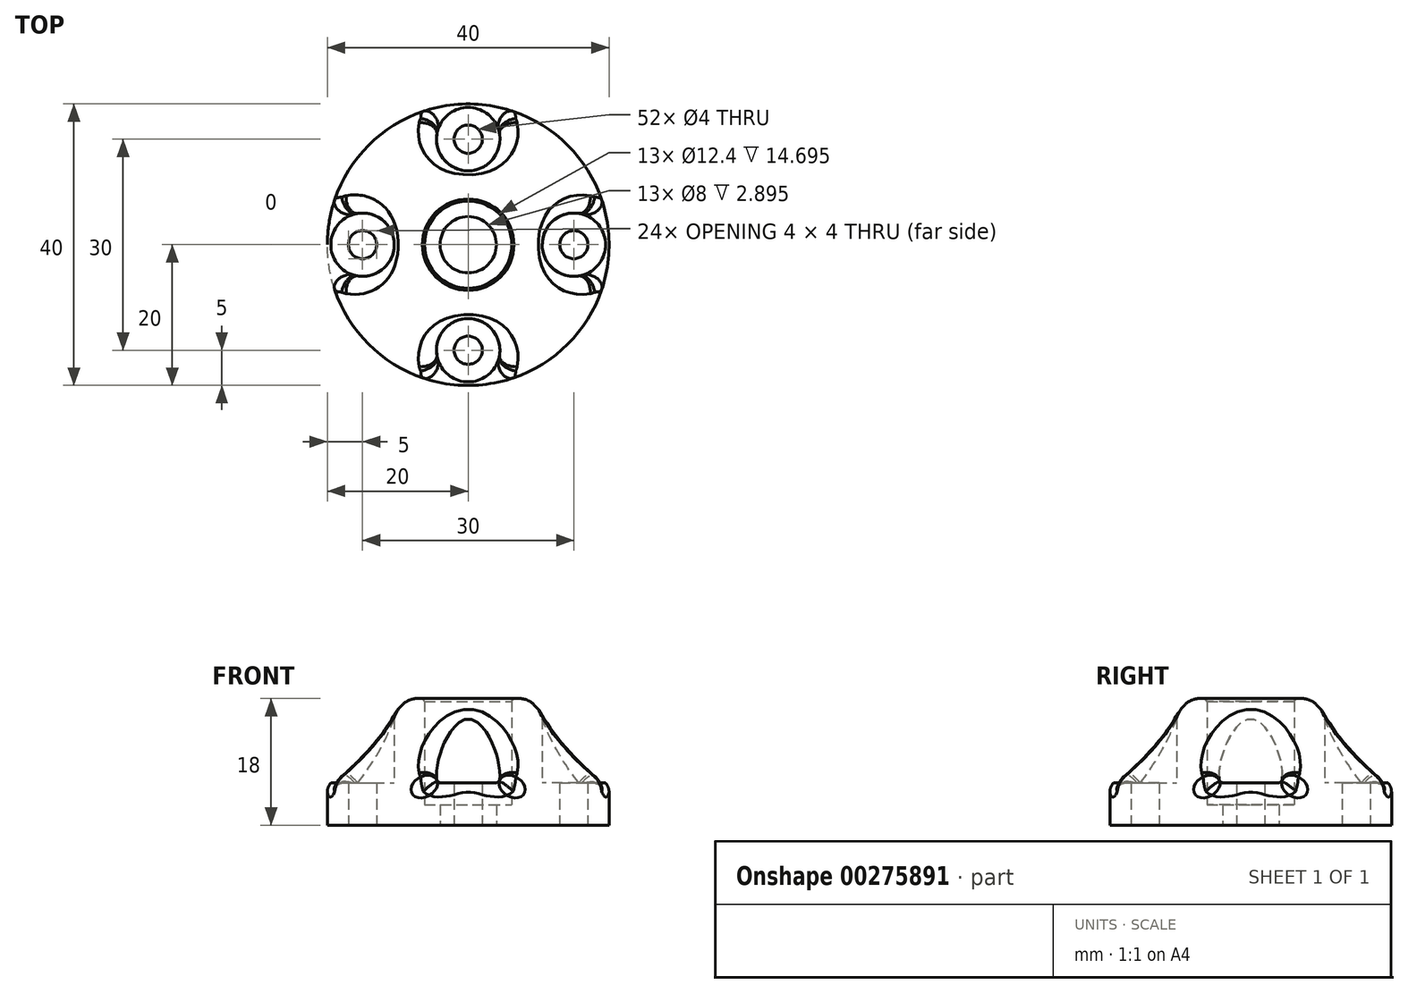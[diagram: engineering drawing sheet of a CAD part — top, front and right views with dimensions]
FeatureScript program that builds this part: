
annotation { "Feature Type Name" : "Feature", "Feature Type Description" : "" }
export const myFeature = defineFeature(function(context is Context, id is Id, definition is map)
    precondition{}
    {
        {
            var Q0;
            Q0=qCreatedBy(makeId("Front.planeOp"),FACE);
            var sketch = newSketch(context, id + "F0", { "sketchPlane" : qUnion([Q0])});
            skLineSegment(sketch, "E0", {"start": v(6.5, 18) * mm, "end": v(8.5, 18) * mm});
            skLineSegment(sketch, "E1", {"start": v(8.5, 18) * mm, "end": v(20, 6) * mm});
            skLineSegment(sketch, "E2", {"start": v(20, 6) * mm, "end": v(20, 0) * mm});
            skLineSegment(sketch, "E3", {"start": v(20, 0) * mm, "end": v(6.1, 0) * mm});
            skLineSegment(sketch, "E4.bottom", {"start": v(6.1, 0) * mm, "end": v(4, 0) * mm});
            skLineSegment(sketch, "E4.top", {"start": v(6.2, 2.9) * mm, "end": v(4, 2.9) * mm});
            skLineSegment(sketch, "E4.right", {"start": v(4, 0) * mm, "end": v(4, 2.9) * mm});
            skLineSegment(sketch, "E5", {"start": v(6.2, 2.9) * mm, "end": v(6.2, 17.59) * mm});
            skLineSegment(sketch, "E6", {"start": v(6.2, 17.59) * mm, "end": v(6.5, 18) * mm});
            skLineSegment(sketch, "E7", {"start": v(0, -10.1) * mm, "end": v(0, 33.45) * mm});
            skSolve(sketch);
        }
        {
            var Q0;
            Q0=makeQuery(id+"F0.imprint","IMPRINT",FACE,{"disambiguationData":[TD([[makeQuery(id+"F0.imprint","IMPRINT",EDGE,{"derivedFrom":sQuery(id+"F0.wireOp",EDGE,"E0")}),-1.0]])]});
            var Q1;
            Q1=sQuery(id+"F0.wireOp",EDGE,"E7");
            revolve(context, id + "F1", {"entities" : qUnion([Q0]), "axis" : qUnion([Q1]), "revolveType" : RevolveType.FULL});
        }
        {
            var Q0;
            Q0=makeQuery(id+"F1.opRevolve","SWEPT_EDGE",EDGE,{"disambiguationData":[OSD([sQuery(id+"F0.wireOp",EDGE,"E0"),sQuery(id+"F0.wireOp",EDGE,"E1")])]});
            fillet(context, id + "F2", {"entities" : qUnion([Q0]), "radius" : 3 * mm, "tangentPropagation" : true, "allowEdgeOverflow" : false});
        }
        {
            var Q0;
            Q0=makeQuery(id+"F1.opRevolve","SWEPT_FACE",FACE,{"disambiguationData":[OSD([sQuery(id+"F0.wireOp",EDGE,"E3"),sQuery(id+"F0.wireOp",EDGE,"E4.bottom")])]});
            cPlane(context, id + "F3", {"entities" : qUnion([Q0]), "cplaneType" : CPlaneType.OFFSET, "offset" : 6 * mm, "oppositeDirection" : true, "width" : 150 * mm, "height" : 150 * mm});
        }
        {
            var Q0;
            Q0=qCreatedBy(id+"F3.planeOp",FACE);
            var sketch = newSketch(context, id + "F4", { "sketchPlane" : qUnion([Q0])});
            skCircle(sketch, "E8", {"center": v(0, 15) * mm, "radius": 4.5 * mm});
            skCircle(sketch, "E9", {"center": v(0, 15) * mm, "radius": 2 * mm});
            skCircle(sketch, "E10.1.0", {"center": v(15, 0) * mm, "radius": 4.5 * mm});
            skCircle(sketch, "E10.1.1", {"center": v(15, 0) * mm, "radius": 2 * mm});
            skCircle(sketch, "E10.2.0", {"center": v(0, -15) * mm, "radius": 4.5 * mm});
            skCircle(sketch, "E10.2.1", {"center": v(0, -15) * mm, "radius": 2 * mm});
            skCircle(sketch, "E10.3.0", {"center": v(-15, 0) * mm, "radius": 4.5 * mm});
            skCircle(sketch, "E10.3.1", {"center": v(-15, 0) * mm, "radius": 2 * mm});
            skPoint(sketch, "E10.center", {"position": v(0, 0) * mm});
            skLineSegment(sketch, "E10.anchor1", {"start": v(0, 0) * mm, "end": v(0, 15) * mm, "construction": true});
            skLineSegment(sketch, "E10.anchor2", {"start": v(0, 0) * mm, "end": v(-15, 0) * mm, "construction": true});
            skSolve(sketch);
        }
        {
            var Q0;
            Q0=makeQuery(id+"F4.imprint","IMPRINT",FACE,{"disambiguationData":[TD([[makeQuery(id+"F4.imprint","IMPRINT",EDGE,{"derivedFrom":sQuery(id+"F4.wireOp",EDGE,"E9")}),1.0]])]});
            var Q1;
            Q1=makeQuery(id+"F4.imprint","IMPRINT",FACE,{"disambiguationData":[TD([[makeQuery(id+"F4.imprint","IMPRINT",EDGE,{"derivedFrom":sQuery(id+"F4.wireOp",EDGE,"E10.1.1")}),1.0]])]});
            var Q2;
            Q2=makeQuery(id+"F4.imprint","IMPRINT",FACE,{"disambiguationData":[TD([[makeQuery(id+"F4.imprint","IMPRINT",EDGE,{"derivedFrom":sQuery(id+"F4.wireOp",EDGE,"E10.2.1")}),1.0]])]});
            var Q3;
            Q3=makeQuery(id+"F4.imprint","IMPRINT",FACE,{"disambiguationData":[TD([[makeQuery(id+"F4.imprint","IMPRINT",EDGE,{"derivedFrom":sQuery(id+"F4.wireOp",EDGE,"E10.3.1")}),1.0]])]});
            extrude(context, id + "F5", {"entities" : qUnion([Q0, Q1, Q2, Q3]), "operationType" : NewBodyOperationType.REMOVE, "oppositeDirection" : true, "depth" : 30 * mm, "symmetric" : true});
        }
        {
            var Q0;
            Q0 = qSketchRegion(id + "F4", true);
            extrude(context, id + "F6", {"entities" : qUnion([Q0]), "operationType" : NewBodyOperationType.REMOVE, "oppositeDirection" : true, "depth" : 15 * mm});
        }
        {
            var Q0;
            Q0=makeQuery(id+"F1.opRevolve","SWEPT_EDGE",EDGE,{"disambiguationData":[OSD([sQuery(id+"F0.wireOp",EDGE,"E1"),sQuery(id+"F0.wireOp",EDGE,"E2")])]});
            fillet(context, id + "F7", {"entities" : qUnion([Q0]), "radius" : 3 * mm, "tangentPropagation" : true, "allowEdgeOverflow" : false});
        }
        {
            var Q0;
            Q0=makeQuery(id+"F6.boolean.opBoolean","INTERSECT",EDGE,{"derivedFrom":[makeQuery(id+"F1.opRevolve","SWEPT_FACE",FACE,{"disambiguationData":[OSD([sQuery(id+"F0.wireOp",EDGE,"E1")])]}),makeQuery(id+"F6.opExtrude","SWEPT_FACE",FACE,{"disambiguationData":[OSD([sQuery(id+"F4.wireOp",EDGE,"E10.3.0")])]})]});
            var Q1;
            Q1=makeQuery(id+"F6.boolean.opBoolean","INTERSECT",EDGE,{"derivedFrom":[makeQuery(id+"F1.opRevolve","SWEPT_FACE",FACE,{"disambiguationData":[OSD([sQuery(id+"F0.wireOp",EDGE,"E1")])]}),makeQuery(id+"F6.opExtrude","SWEPT_FACE",FACE,{"disambiguationData":[OSD([sQuery(id+"F4.wireOp",EDGE,"E8")])]})]});
            var Q2;
            Q2=makeQuery(id+"F6.boolean.opBoolean","INTERSECT",EDGE,{"derivedFrom":[makeQuery(id+"F1.opRevolve","SWEPT_FACE",FACE,{"disambiguationData":[OSD([sQuery(id+"F0.wireOp",EDGE,"E1")])]}),makeQuery(id+"F6.opExtrude","SWEPT_FACE",FACE,{"disambiguationData":[OSD([sQuery(id+"F4.wireOp",EDGE,"E10.1.0")])]})]});
            var Q3;
            Q3=makeQuery(id+"F6.boolean.opBoolean","INTERSECT",EDGE,{"derivedFrom":[makeQuery(id+"F1.opRevolve","SWEPT_FACE",FACE,{"disambiguationData":[OSD([sQuery(id+"F0.wireOp",EDGE,"E1")])]}),makeQuery(id+"F6.opExtrude","SWEPT_FACE",FACE,{"disambiguationData":[OSD([sQuery(id+"F4.wireOp",EDGE,"E10.2.0")])]})]});
            fillet(context, id + "F8", {"entities" : qUnion([Q0, Q1, Q2, Q3]), "radius" : 2 * mm, "tangentPropagation" : true, "allowEdgeOverflow" : false});
        }
    });
